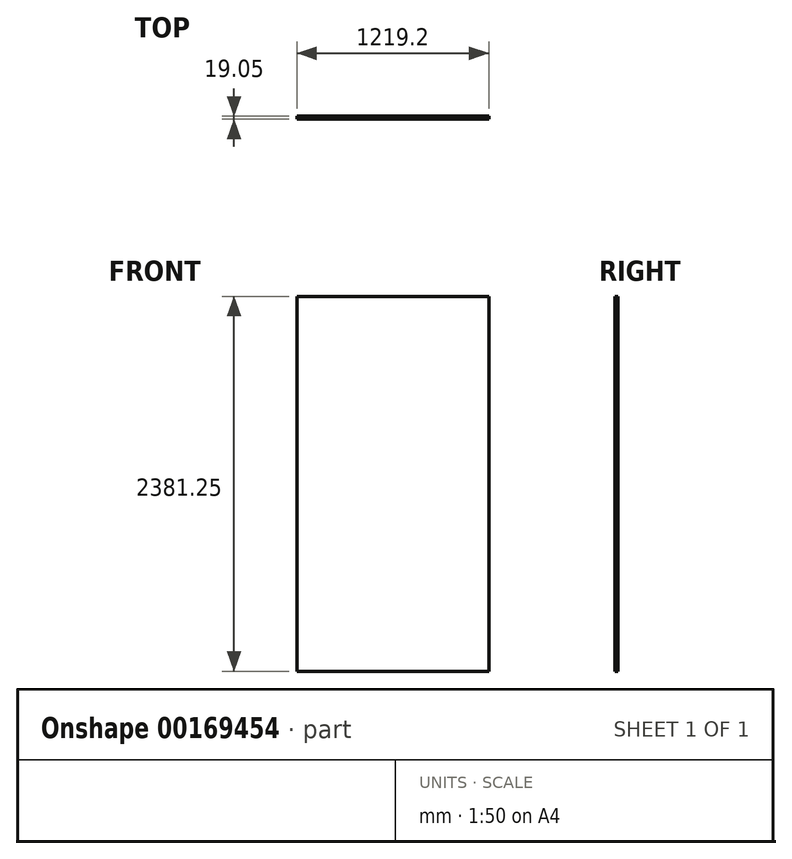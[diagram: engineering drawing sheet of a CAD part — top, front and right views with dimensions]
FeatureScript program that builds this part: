
annotation { "Feature Type Name" : "Feature", "Feature Type Description" : "" }
export const myFeature = defineFeature(function(context is Context, id is Id, definition is map)
    precondition{}
    {
        {
            var Q0;
            Q0=qCreatedBy(makeId("Front.planeOp"),FACE);
            var sketch = newSketch(context, id + "F0", { "sketchPlane" : qUnion([Q0])});
            skLineSegment(sketch, "E0.bottom", {"start": v(-373.4, 1541.79) * mm, "end": v(845.8, 1541.79) * mm});
            skLineSegment(sketch, "E0.top", {"start": v(-373.4, -839.46) * mm, "end": v(845.8, -839.46) * mm});
            skLineSegment(sketch, "E0.left", {"start": v(-373.4, 1541.79) * mm, "end": v(-373.4, -839.46) * mm});
            skLineSegment(sketch, "E0.right", {"start": v(845.8, 1541.79) * mm, "end": v(845.8, -839.46) * mm});
            skSolve(sketch);
        }
        {
            var Q0;
            Q0 = qSketchRegion(id + "F0", true);
            extrude(context, id + "F1", {"entities" : qUnion([Q0]), "depth" : 19.05 * mm});
        }
    });
